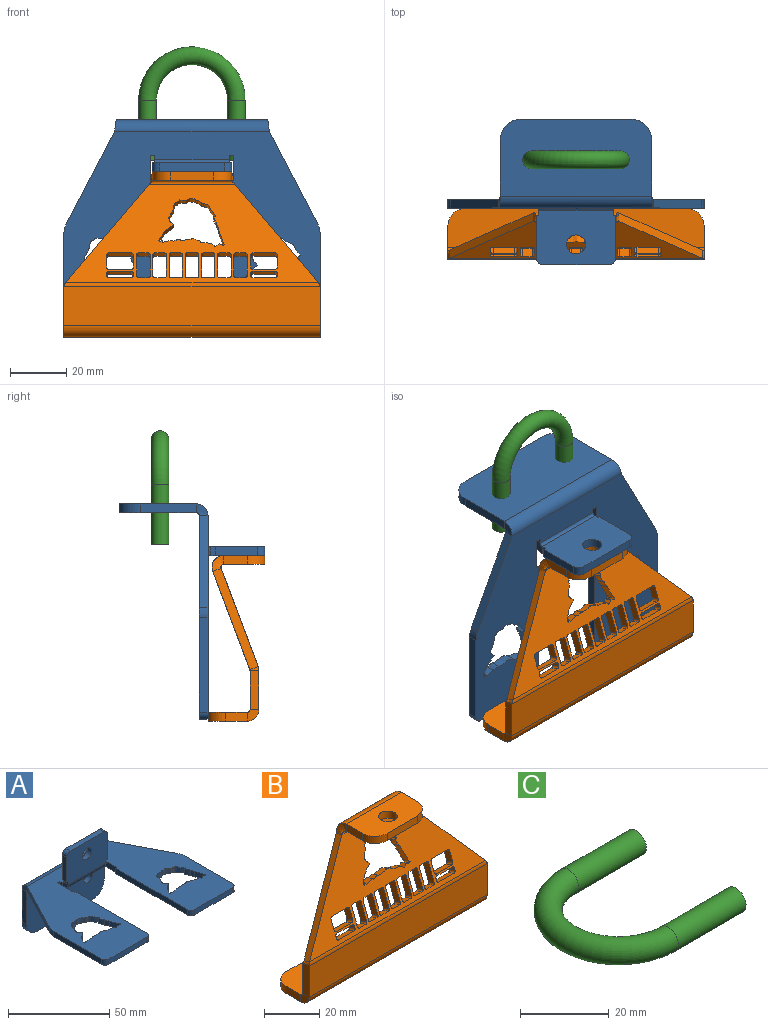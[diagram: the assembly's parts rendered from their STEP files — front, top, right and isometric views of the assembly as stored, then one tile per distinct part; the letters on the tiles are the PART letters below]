
ASSEMBLY  parts=3 mates=2
PART A: 137 faces, bbox 91.4x76.8x52.1 mm
  f0: extruded ~3.18x1.23mm, area 5mm2, adj f1,f118,f122,f127
  f1: extruded ~3.18x0.29mm, area 1.3mm2, adj f0,f2,f122,f127
  f2: plane 3.18x0.73mm, normal (0.99,-0.11,0), area 2.3mm2, adj f1,f3,f122,f127
  f3: plane 3.18x0.12mm, normal (0.16,-0.99,0), area 0.4mm2, adj f2,f4,f122,f127
  f4: extruded ~3.18x1.76mm, area 5.8mm2, adj f3,f5,f122,f127
  f5: extruded ~5.06x3.18mm, area 18.6mm2, adj f4,f6,f122,f127
  f6: plane 3.18x0.22mm, normal (-0.34,0.94,0), area 0.7mm2, adj f5,f7,f122,f127
  f7: plane 3.18x0.96mm, normal (0.85,0.53,0), area 3.6mm2, adj f6,f8,f122,f127
  f8: extruded ~3.67x3.18mm, area 14.9mm2, adj f7,f9,f122,f127
  f9: extruded ~3.37x3.18mm, area 12.2mm2, adj f8,f10,f122,f127
  f10: plane 3.18x0.41mm, normal (0.8,0.61,0), area 1.6mm2, adj f9,f11,f122,f127
  f11: extruded ~3.18x1.02mm, area 3.7mm2, adj f10,f12,f122,f127
  f12: extruded ~3.18x0.67mm, area 2.2mm2, adj f11,f13,f122,f127
  f13: plane 3.49x3.18mm, normal (-0.25,0.97,0), area 11.4mm2, adj f12,f14,f122,f127
  f14: plane 3.18x0.45mm, normal (0.69,0.72,0), area 2mm2, adj f13,f15,f122,f127
  f15: extruded ~3.18x2.35mm, area 7.8mm2, adj f14,f16,f122,f127
  f16: extruded ~7.55x3.18mm, area 26.4mm2, adj f15,f17,f122,f127
  f17: extruded ~3.18x0.31mm, area 1.1mm2, adj f16,f18,f122,f127
  f18: extruded ~5.49x3.18mm, area 19.8mm2, adj f17,f19,f122,f127
  f19: plane 3.18x1.27mm, normal (-0.64,0.77,0), area 5.3mm2, adj f18,f20,f122,f127
  f20: plane 3.18x1.51mm, normal (0.36,0.93,0), area 5.1mm2, adj f19,f21,f122,f127
  f21: plane 3.18x0.49mm, normal (-0.75,0.66,0), area 2.1mm2, adj f20,f22,f122,f127
  f22: extruded ~5.47x3.18mm, area 19mm2, adj f21,f23,f122,f127
  f23: plane 3.18x0.06mm, normal (-0.83,0.55,0), area 0.2mm2, adj f22,f24,f122,f127
  f24: plane 3.18x2.27mm, normal (-0.95,-0.33,0), area 7.6mm2, adj f23,f25,f122,f127
  f25: plane 3.18x0.08mm, normal (-0.71,0.71,0), area 0.4mm2, adj f24,f26,f122,f127
  f26: extruded ~3.18x2.84mm, area 10mm2, adj f25,f27,f122,f127
  f27: extruded ~3.18x0.8mm, area 3mm2, adj f26,f28,f122,f127
  f28: extruded ~4.31x3.18mm, area 16.9mm2, adj f27,f29,f122,f127
  f29: extruded ~3.18x1.2mm, area 3.9mm2, adj f28,f30,f122,f127
  f30: plane 3.18x0.16mm, normal (-0.89,-0.45,0), area 0.6mm2, adj f29,f31,f122,f127
  f31: plane 3.18x0.84mm, normal (-0.07,-1,0), area 2.7mm2, adj f30,f32,f122,f127
  f32: extruded ~3.18x1.27mm, area 5.5mm2, adj f31,f33,f122,f127
  f33: plane 3.18x0.04mm, normal (-0.89,0.45,0), area 0.1mm2, adj f32,f34,f122,f127
  f34: plane 3.18x0.76mm, normal (-0.34,-0.94,0), area 2.6mm2, adj f33,f35,f122,f127
  f35: plane 3.18x0.04mm, normal (-0.89,0.45,0), area 0.1mm2, adj f34,f36,f122,f127
  f36: extruded ~3.18x2.14mm, area 6.9mm2, adj f35,f37,f122,f127
  f37: plane 3.18x0.16mm, normal (-0.99,-0.12,0), area 0.5mm2, adj f36,f38,f122,f127
  f38: plane 3.18x0.2mm, normal (-0.51,-0.86,0), area 0.7mm2, adj f37,f39,f122,f127
  f39: extruded ~3.63x3.18mm, area 12.4mm2, adj f38,f40,f122,f127
  f40: plane 3.18x0.18mm, normal (0.91,-0.41,0), area 0.6mm2, adj f39,f118,f122,f127
  f41: plane 3.18x0.47mm, normal (-0.73,0.68,0), area 2mm2, adj f42,f117,f122,f127
  f42: extruded ~5.47x3.18mm, area 19mm2, adj f41,f43,f122,f127
  f43: plane 3.18x0.06mm, normal (-0.83,0.55,0), area 0.2mm2, adj f42,f44,f122,f127
  f44: plane 3.18x2.27mm, normal (-0.95,-0.33,0), area 7.6mm2, adj f43,f45,f122,f127
  f45: plane 3.18x0.08mm, normal (-0.71,0.71,0), area 0.4mm2, adj f44,f46,f122,f127
  f46: extruded ~3.18x2.84mm, area 10mm2, adj f45,f47,f122,f127
  f47: extruded ~3.18x0.8mm, area 3mm2, adj f46,f48,f122,f127
  f48: extruded ~4.31x3.18mm, area 16.9mm2, adj f47,f49,f122,f127
  f49: extruded ~3.18x1.2mm, area 3.9mm2, adj f48,f50,f122,f127
  f50: plane 3.18x0.16mm, normal (-0.89,-0.45,0), area 0.6mm2, adj f49,f51,f122,f127
  f51: plane 3.18x0.84mm, normal (-0.07,-1,0), area 2.7mm2, adj f50,f52,f122,f127
  f52: extruded ~3.18x1.27mm, area 5.5mm2, adj f51,f53,f122,f127
  f53: plane 3.18x0.04mm, normal (-0.89,0.45,0), area 0.1mm2, adj f52,f54,f122,f127
  f54: plane 3.18x0.76mm, normal (-0.34,-0.94,0), area 2.6mm2, adj f53,f55,f122,f127
  f55: plane 3.18x0.04mm, normal (-0.89,0.45,0), area 0.1mm2, adj f54,f56,f122,f127
  f56: extruded ~3.18x2.14mm, area 6.9mm2, adj f55,f57,f122,f127
  f57: plane 3.18x0.16mm, normal (-0.99,-0.12,0), area 0.5mm2, adj f56,f58,f122,f127
  f58: plane 3.18x0.2mm, normal (-0.51,-0.86,0), area 0.7mm2, adj f57,f59,f122,f127
  f59: extruded ~3.63x3.18mm, area 12.4mm2, adj f58,f60,f122,f127
  f60: plane 3.18x0.18mm, normal (0.91,-0.41,0), area 0.6mm2, adj f59,f61,f122,f127
  f61: plane 3.18x0.14mm, normal (-0.27,-0.96,0), area 0.5mm2, adj f60,f62,f122,f127
  f62: extruded ~3.18x1.24mm, area 5mm2, adj f61,f63,f122,f127
  f63: extruded ~3.18x0.29mm, area 1.3mm2, adj f62,f64,f122,f127
  f64: plane 3.18x0.73mm, normal (0.99,-0.11,0), area 2.3mm2, adj f63,f65,f122,f127
  f65: plane 3.18x0.12mm, normal (0.16,-0.99,0), area 0.4mm2, adj f64,f66,f122,f127
  f66: extruded ~3.18x1.76mm, area 5.8mm2, adj f65,f67,f122,f127
  f67: extruded ~5.06x3.18mm, area 18.6mm2, adj f66,f68,f122,f127
  f68: plane 3.18x0.22mm, normal (-0.34,0.94,0), area 0.7mm2, adj f67,f69,f122,f127
  f69: plane 3.18x0.96mm, normal (0.85,0.53,0), area 3.6mm2, adj f68,f70,f122,f127
  f70: extruded ~3.67x3.18mm, area 14.9mm2, adj f69,f71,f122,f127
  f71: extruded ~3.37x3.18mm, area 12.2mm2, adj f70,f72,f122,f127
  f72: plane 3.18x0.41mm, normal (0.8,0.61,0), area 1.6mm2, adj f71,f73,f122,f127
  f73: extruded ~3.18x1.02mm, area 3.7mm2, adj f72,f74,f122,f127
  f74: extruded ~3.18x0.67mm, area 2.2mm2, adj f73,f75,f122,f127
  f75: plane 3.49x3.18mm, normal (-0.25,0.97,0), area 11.4mm2, adj f74,f76,f122,f127
  f76: plane 3.18x0.45mm, normal (0.69,0.72,0), area 2mm2, adj f75,f77,f122,f127
  f77: extruded ~3.18x2.35mm, area 7.8mm2, adj f76,f78,f122,f127
  f78: extruded ~7.55x3.18mm, area 26.4mm2, adj f77,f79,f122,f127
  f79: extruded ~3.18x0.31mm, area 1.1mm2, adj f78,f80,f122,f127
  f80: extruded ~5.49x3.18mm, area 19.8mm2, adj f79,f81,f122,f127
  f81: plane 3.18x1.27mm, normal (-0.64,0.76,0), area 5.3mm2, adj f80,f117,f122,f127
  f82: plane 3.18x1.59mm, normal (-1,0,0), area 5mm2, adj f83,f119,f122,f127
  f83: plane 3.18x1.59mm, normal (0,-1,0), area 5mm2, adj f82,f84,f122,f127
  f84: plane 11.56x3.18mm, normal (1,0,0), area 36.7mm2, adj f83,f85,f122,f127
  f85: plane 3.18x0.79mm, normal (0,1,0), area 2.5mm2, adj f84,f86,f122,f127
  f86: plane 50.1x3.18mm, normal (1,0,0), area 159.1mm2, adj f85,f87,f122,f127
  f87: cylinder r=2.54mm len=3.18mm, axis (0,0,1), area 12.7mm2, adj f86,f88,f122,f127
  f88: plane 26.51x3.18mm, normal (0,-1,0), area 84.2mm2, adj f87,f89,f122,f127
  f89: cylinder r=2.54mm len=3.18mm, axis (0,0,1), area 12.7mm2, adj f88,f90,f122,f127
  f90: plane 33.68x3.18mm, normal (-1,0,0), area 106.9mm2, adj f89,f122,f127,f131
  f91: plane 32.88x17.24mm, normal (-0.89,0.46,0), area 117.9mm2, adj f92,f122,f127,f131
  f92: bspline ~5.02x4.76mm, area 13.1mm2, adj f91,f93,f124,f129
  f93: plane 19.94x3.18mm, normal (-1,0,0), area 63.3mm2, adj f92,f121,f126,f133
  f94: plane 38.91x3.18mm, normal (0,0,-1), area 123.5mm2, adj f121,f126,f132,f133
  f95: plane 19.94x3.18mm, normal (1,0,0), area 63.3mm2, adj f96,f121,f126,f132
  f96: bspline ~5.2x5.02mm, area 13.1mm2, adj f95,f97,f124,f129
  f97: plane 32.88x17.24mm, normal (0.89,0.46,0), area 117.9mm2, adj f96,f122,f127,f130
  f98: plane 33.68x3.18mm, normal (1,0,0), area 106.9mm2, adj f99,f122,f127,f130
  f99: cylinder r=2.54mm len=3.18mm, axis (0,0,1), area 12.7mm2, adj f98,f100,f122,f127
  f100: plane 26.51x3.18mm, normal (0,-1,0), area 84.2mm2, adj f99,f101,f122,f127
  f101: cylinder r=2.54mm len=3.18mm, axis (0,0,1), area 12.7mm2, adj f100,f102,f122,f127
  f102: plane 50.1x3.18mm, normal (-1,0,0), area 159.1mm2, adj f101,f103,f122,f127
  f103: plane 3.18x0.79mm, normal (0,1,0), area 2.5mm2, adj f102,f104,f122,f127
  f104: plane 11.56x3.18mm, normal (-1,0,0), area 36.7mm2, adj f103,f105,f122,f127
  f105: plane 3.18x1.59mm, normal (0,-1,0), area 5mm2, adj f104,f106,f122,f127
  f106: plane 3.18x1.59mm, normal (1,0,0), area 5mm2, adj f105,f107,f122,f127
  f107: plane 4.19x4.19mm, normal (1,0,0), area 13mm2, adj f106,f108,f123,f128
  f108: plane 3.18x1.59mm, normal (1,0,0), area 5mm2, adj f107,f109,f120,f125
  f109: plane 3.18x0.79mm, normal (0,0,-1), area 2.5mm2, adj f108,f110,f120,f125
  f110: plane 15.18x3.18mm, normal (1,0,0), area 48.2mm2, adj f109,f111,f120,f125
  f111: cylinder r=2.54mm len=3.18mm, axis (0,1,0), area 12.7mm2, adj f110,f112,f120,f125
  f112: plane 23.18x3.18mm, normal (0,0,1), area 73.6mm2, adj f111,f113,f120,f125
  f113: cylinder r=2.54mm len=3.18mm, axis (0,1,0), area 12.7mm2, adj f112,f114,f120,f125
  f114: plane 15.18x3.18mm, normal (-1,0,0), area 48.2mm2, adj f113,f115,f120,f125
  f115: plane 3.18x0.79mm, normal (0,0,-1), area 2.5mm2, adj f114,f116,f120,f125
  f116: plane 3.18x1.59mm, normal (-1,0,0), area 5mm2, adj f115,f119,f120,f125
  f117: plane 3.18x1.51mm, normal (0.36,0.93,0), area 5.1mm2, adj f41,f81,f122,f127
  f118: plane 3.18x0.14mm, normal (-0.27,-0.96,0), area 0.5mm2, adj f0,f40,f122,f127
  f119: plane 4.19x4.19mm, normal (-1,0,0), area 13mm2, adj f82,f116,f123,f128
  f120: plane 28.26x19.3mm, normal (0,-1,0), area 504.4mm2, adj f108,f109,f110,f111,f112,f113,f114,f115
  f121: plane 54.15x27.56mm, normal (0,-1,0), area 1415.7mm2, adj f93,f94,f95,f124,f132,f133,f134,f135
  f122: plane 91.44x72.64mm, normal (0,0,-1), area 3734.6mm2, adj f0,f1,f2,f3,f4,f5,f6,f7
  f123: cylinder r=4.19mm len=26.68mm, axis (1,0,0), area 175.6mm2, adj f107,f119,f120,f122
  f124: cylinder r=1.02mm len=55.22mm, axis (1,0,0), area 87mm2, adj f92,f96,f121,f122
  f125: plane 28.26x19.3mm, normal (0,1,0), area 504.4mm2, adj f108,f109,f110,f111,f112,f113,f114,f115
  f126: plane 54.15x27.56mm, normal (0,1,0), area 1415.7mm2, adj f93,f94,f95,f129,f132,f133,f134,f135
  f127: plane 91.44x72.64mm, normal (0,0,1), area 3734.6mm2, adj f0,f1,f2,f3,f4,f5,f6,f7
  f128: cylinder r=1.02mm len=26.68mm, axis (1,0,0), area 42.6mm2, adj f107,f119,f125,f127
  f129: cylinder r=4.19mm len=55.22mm, axis (1,0,0), area 359mm2, adj f92,f96,f126,f127
  f130: cylinder r=7.62mm len=3.54mm, axis (0,0,1), area 11.7mm2, adj f97,f98,f122,f127
  f131: cylinder r=7.62mm len=3.54mm, axis (0,0,-1), area 11.7mm2, adj f90,f91,f122,f127
  f132: cylinder r=7.62mm len=7.62mm, axis (0,-1,0), area 38mm2, adj f94,f95,f121,f126
  f133: cylinder r=7.62mm len=7.62mm, axis (0,1,0), area 38mm2, adj f93,f94,f121,f126
  f134: cylinder r=2.87mm len=5.74mm, axis (0,1,0), area 57.3mm2, adj f121,f126
  f135: cylinder r=2.87mm len=5.74mm, axis (0,1,0), area 57.3mm2, adj f121,f126
  f136: cylinder r=3.38mm len=6.76mm, axis (0,1,0), area 67.4mm2, adj f120,f125
PART B: 165 faces, bbox 91.4x20.6x59.1 mm
  f0: bspline ~5.67x4.19mm, area 16.5mm2, adj f3,f16,f22,f163
  f1: bspline ~6.5x5.91mm, area 16.5mm2, adj f3,f6,f22,f164
  f2: plane 28.26x14.68mm, normal (0,0,1), area 361.9mm2, adj f3,f4,f5,f17,f118,f163,f164
  f3: cylinder r=4.19mm len=30.6mm, axis (1,0,0), area 235.9mm2, adj f0,f1,f2,f25
  f4: cylinder r=6.35mm len=6.35mm, axis (0,0,1), area 31.7mm2, adj f2,f17,f18,f163
  f5: cylinder r=6.35mm len=6.35mm, axis (0,0,1), area 31.7mm2, adj f2,f17,f18,f164
  f6: plane 36.22x29.81mm, normal (-0.78,0.22,0.58), area 152.1mm2, adj f1,f7,f19,f25
  f7: bspline ~3.26x1.64mm, area 3.7mm2, adj f6,f8,f23,f28
  f8: plane 13.8x3.18mm, normal (-1,0,0), area 43.8mm2, adj f7,f9,f20,f26
  f9: plane 4.19x4.19mm, normal (-1,0,0), area 13mm2, adj f8,f10,f24,f29
  f10: plane 7.63x3.18mm, normal (-1,0,0), area 24.2mm2, adj f9,f21,f27,f162
  f11: plane 78.74x3.18mm, normal (0,1,0), area 250mm2, adj f21,f27,f161,f162
  f12: plane 7.63x3.18mm, normal (1,0,0), area 24.2mm2, adj f13,f21,f27,f161
  f13: plane 4.19x4.19mm, normal (1,0,0), area 13mm2, adj f12,f14,f24,f29
  f14: plane 13.8x3.18mm, normal (1,0,0), area 43.8mm2, adj f13,f15,f20,f26
  f15: bspline ~3.26x1.77mm, area 3.7mm2, adj f14,f16,f23,f28
  f16: plane 36.22x29.81mm, normal (0.78,0.22,0.58), area 152.1mm2, adj f0,f15,f19,f25
  f17: plane 15.56x3.18mm, normal (0,-1,0), area 49.4mm2, adj f2,f4,f5,f18
  f18: plane 28.26x14.68mm, normal (0,0,-1), area 361.9mm2, adj f4,f5,f17,f22,f118,f163,f164
  f19: plane 90.23x35.1mm, normal (0,-0.94,0.35), area 1523mm2, adj f6,f16,f22,f23,f30,f31,f32,f33
  f20: plane 91.44x13.8mm, normal (0,-1,0), area 1261.8mm2, adj f8,f14,f23,f24
  f21: plane 91.44x13.98mm, normal (0,0,-1), area 1261.4mm2, adj f10,f11,f12,f24,f161,f162
  f22: cylinder r=1.02mm len=30.6mm, axis (1,0,0), area 57.2mm2, adj f0,f1,f18,f19
  f23: cylinder r=4.19mm len=91.44mm, axis (-1,0,0), area 137.4mm2, adj f7,f15,f19,f20
  f24: cylinder r=4.19mm len=91.44mm, axis (-1,0,0), area 602mm2, adj f9,f13,f20,f21
  f25: plane 90.23x35.1mm, normal (0,0.94,-0.35), area 1518.8mm2, adj f3,f6,f16,f28,f30,f31,f32,f33
  f26: plane 91.44x13.8mm, normal (0,1,0), area 1261.8mm2, adj f8,f14,f28,f29
  f27: plane 91.44x13.98mm, normal (0,0,1), area 1261.4mm2, adj f10,f11,f12,f29,f161,f162
  f28: cylinder r=1.02mm len=91.44mm, axis (-1,0,0), area 33.3mm2, adj f7,f15,f25,f26
  f29: cylinder r=1.02mm len=91.44mm, axis (-1,0,0), area 145.9mm2, adj f9,f13,f26,f27
  f30: plane 3.37x2.97mm, normal (0,0.35,0.94), area 10.7mm2, adj f19,f25,f31,f37
  f31: cylinder r=0.69mm len=3.21mm, axis (0,-0.94,0.35), area 3.4mm2, adj f19,f25,f30,f32
  f32: plane 8.76x5.85mm, normal (-1,0,0), area 25.9mm2, adj f19,f25,f31,f33
  f33: cylinder r=0.69mm len=3.21mm, axis (0,-0.94,0.35), area 3.4mm2, adj f19,f25,f32,f34
  f34: plane 3.37x2.97mm, normal (0,-0.35,-0.94), area 10.7mm2, adj f19,f25,f33,f35
  f35: cylinder r=0.69mm len=3.21mm, axis (0,-0.94,0.35), area 3.4mm2, adj f19,f25,f34,f36
  f36: plane 8.76x5.85mm, normal (1,0,0), area 25.9mm2, adj f19,f25,f35,f37
  f37: cylinder r=0.69mm len=3.21mm, axis (0,-0.94,0.35), area 3.4mm2, adj f19,f25,f30,f36
  f38: plane 3.37x2.97mm, normal (0,-0.35,-0.94), area 10.7mm2, adj f19,f25,f39,f45
  f39: cylinder r=0.69mm len=3.21mm, axis (0,-0.94,0.35), area 3.4mm2, adj f19,f25,f38,f40
  f40: plane 8.76x5.85mm, normal (1,0,0), area 25.9mm2, adj f19,f25,f39,f41
  f41: cylinder r=0.69mm len=3.21mm, axis (0,-0.94,0.35), area 3.4mm2, adj f19,f25,f40,f42
  f42: plane 3.37x2.97mm, normal (0,0.35,0.94), area 10.7mm2, adj f19,f25,f41,f43
  f43: cylinder r=0.69mm len=3.21mm, axis (0,-0.94,0.35), area 3.4mm2, adj f19,f25,f42,f44
  f44: plane 8.76x5.85mm, normal (-1,0,0), area 25.9mm2, adj f19,f25,f43,f45
  f45: cylinder r=0.69mm len=3.21mm, axis (0,-0.94,0.35), area 3.4mm2, adj f19,f25,f38,f44
  f46: plane 8.76x5.85mm, normal (1,0,0), area 25.9mm2, adj f19,f25,f47,f53
  f47: cylinder r=0.69mm len=3.21mm, axis (0,-0.94,0.35), area 3.4mm2, adj f19,f25,f46,f48
  f48: plane 3.37x2.97mm, normal (0,0.35,0.94), area 10.7mm2, adj f19,f25,f47,f49
  f49: cylinder r=0.69mm len=3.21mm, axis (0,-0.94,0.35), area 3.4mm2, adj f19,f25,f48,f50
  f50: plane 8.76x5.85mm, normal (-1,0,0), area 25.9mm2, adj f19,f25,f49,f51
  f51: cylinder r=0.69mm len=3.21mm, axis (0,-0.94,0.35), area 3.4mm2, adj f19,f25,f50,f52
  f52: plane 3.37x2.97mm, normal (0,-0.35,-0.94), area 10.7mm2, adj f19,f25,f51,f53
  f53: cylinder r=0.69mm len=3.21mm, axis (0,-0.94,0.35), area 3.4mm2, adj f19,f25,f46,f52
  f54: plane 3.37x2.97mm, normal (0,0.35,0.94), area 10.7mm2, adj f19,f25,f55,f61
  f55: cylinder r=0.69mm len=3.21mm, axis (0,-0.94,0.35), area 3.4mm2, adj f19,f25,f54,f56
  f56: plane 8.76x5.85mm, normal (-1,0,0), area 25.9mm2, adj f19,f25,f55,f57
  f57: cylinder r=0.69mm len=3.21mm, axis (0,-0.94,0.35), area 3.4mm2, adj f19,f25,f56,f58
  f58: plane 3.37x2.97mm, normal (0,-0.35,-0.94), area 10.7mm2, adj f19,f25,f57,f59
  f59: cylinder r=0.69mm len=3.21mm, axis (0,-0.94,0.35), area 3.4mm2, adj f19,f25,f58,f60
  f60: plane 8.76x5.85mm, normal (1,0,0), area 25.9mm2, adj f19,f25,f59,f61
  f61: cylinder r=0.69mm len=3.21mm, axis (0,-0.94,0.35), area 3.4mm2, adj f19,f25,f54,f60
  f62: plane 3.37x2.97mm, normal (0,0.35,0.94), area 10.7mm2, adj f19,f25,f63,f69
  f63: cylinder r=0.69mm len=3.21mm, axis (0,-0.94,0.35), area 3.4mm2, adj f19,f25,f62,f64
  f64: plane 8.76x5.85mm, normal (-1,0,0), area 25.9mm2, adj f19,f25,f63,f65
  f65: cylinder r=0.69mm len=3.21mm, axis (0,-0.94,0.35), area 3.4mm2, adj f19,f25,f64,f66
  f66: plane 3.37x2.97mm, normal (0,-0.35,-0.94), area 10.7mm2, adj f19,f25,f65,f67
  f67: cylinder r=0.69mm len=3.21mm, axis (0,-0.94,0.35), area 3.4mm2, adj f19,f25,f66,f68
  f68: plane 8.76x5.85mm, normal (1,0,0), area 25.9mm2, adj f19,f25,f67,f69
  f69: cylinder r=0.69mm len=3.21mm, axis (0,-0.94,0.35), area 3.4mm2, adj f19,f25,f62,f68
  f70: plane 3.37x2.97mm, normal (0,-0.35,-0.94), area 10.7mm2, adj f19,f25,f71,f77
  f71: cylinder r=0.69mm len=3.21mm, axis (0,-0.94,0.35), area 3.4mm2, adj f19,f25,f70,f72
  f72: plane 8.76x5.85mm, normal (1,0,0), area 25.9mm2, adj f19,f25,f71,f73
  f73: cylinder r=0.69mm len=3.21mm, axis (0,-0.94,0.35), area 3.4mm2, adj f19,f25,f72,f74
  f74: plane 3.37x2.97mm, normal (0,0.35,0.94), area 10.7mm2, adj f19,f25,f73,f75
  f75: cylinder r=0.69mm len=3.21mm, axis (0,-0.94,0.35), area 3.4mm2, adj f19,f25,f74,f76
  f76: plane 8.76x5.85mm, normal (-1,0,0), area 25.9mm2, adj f19,f25,f75,f77
  f77: cylinder r=0.69mm len=3.21mm, axis (0,-0.94,0.35), area 3.4mm2, adj f19,f25,f70,f76
  f78: plane 3.37x2.97mm, normal (0,-0.35,-0.94), area 10.7mm2, adj f19,f25,f79,f85
  f79: cylinder r=0.69mm len=3.21mm, axis (0,-0.94,0.35), area 3.4mm2, adj f19,f25,f78,f80
  f80: plane 8.76x5.85mm, normal (1,0,0), area 25.9mm2, adj f19,f25,f79,f81
  f81: cylinder r=0.69mm len=3.21mm, axis (0,-0.94,0.35), area 3.4mm2, adj f19,f25,f80,f82
  f82: plane 3.37x2.97mm, normal (0,0.35,0.94), area 10.7mm2, adj f19,f25,f81,f83
  f83: cylinder r=0.69mm len=3.21mm, axis (0,-0.94,0.35), area 3.4mm2, adj f19,f25,f82,f84
  f84: plane 8.76x5.85mm, normal (-1,0,0), area 25.9mm2, adj f19,f25,f83,f85
  f85: cylinder r=0.69mm len=3.21mm, axis (0,-0.94,0.35), area 3.4mm2, adj f19,f25,f78,f84
  f86: plane 7.81x2.97mm, normal (0,0.35,0.94), area 24.8mm2, adj f19,f25,f87,f93
  f87: cylinder r=0.86mm len=3.27mm, axis (0,-0.94,0.35), area 4.3mm2, adj f19,f25,f86,f88
  f88: plane 5.35x4.57mm, normal (-1,0,0), area 14.4mm2, adj f19,f25,f87,f89
  f89: cylinder r=0.86mm len=3.27mm, axis (0,-0.94,0.35), area 4.3mm2, adj f19,f25,f88,f90
  f90: plane 7.81x2.97mm, normal (0,-0.35,-0.94), area 24.8mm2, adj f19,f25,f89,f91
  f91: cylinder r=0.86mm len=3.27mm, axis (0,-0.94,0.35), area 4.3mm2, adj f19,f25,f90,f92
  f92: plane 5.35x4.57mm, normal (1,0,0), area 14.4mm2, adj f19,f25,f91,f93
  f93: cylinder r=0.86mm len=3.27mm, axis (0,-0.94,0.35), area 4.3mm2, adj f19,f25,f86,f92
  f94: plane 7.81x2.97mm, normal (0,0.35,0.94), area 24.8mm2, adj f19,f25,f95,f101
  f95: cylinder r=0.86mm len=3.27mm, axis (0,-0.94,0.35), area 4.3mm2, adj f19,f25,f94,f96
  f96: plane 5.35x4.57mm, normal (-1,0,0), area 14.4mm2, adj f19,f25,f95,f97
  f97: cylinder r=0.86mm len=3.27mm, axis (0,-0.94,0.35), area 4.3mm2, adj f19,f25,f96,f98
  f98: plane 7.81x2.97mm, normal (0,-0.35,-0.94), area 24.8mm2, adj f19,f25,f97,f99
  f99: cylinder r=0.86mm len=3.27mm, axis (0,-0.94,0.35), area 4.3mm2, adj f19,f25,f98,f100
  f100: plane 5.35x4.57mm, normal (1,0,0), area 14.4mm2, adj f19,f25,f99,f101
  f101: cylinder r=0.86mm len=3.27mm, axis (0,-0.94,0.35), area 4.3mm2, adj f19,f25,f94,f100
  f102: plane 7.81x2.97mm, normal (0,-0.35,-0.94), area 24.8mm2, adj f19,f25,f103,f109
  f103: cylinder r=0.86mm len=3.27mm, axis (0,-0.94,0.35), area 4.3mm2, adj f19,f25,f102,f104
  f104: plane 3.26x1.89mm, normal (1,0,0), area 2.6mm2, adj f19,f25,f103,f105
  f105: cylinder r=0.86mm len=3.27mm, axis (0,-0.94,0.35), area 4.3mm2, adj f19,f25,f104,f106
  f106: plane 7.81x2.97mm, normal (0,0.35,0.94), area 24.8mm2, adj f19,f25,f105,f107
  f107: cylinder r=0.86mm len=3.27mm, axis (0,-0.94,0.35), area 4.3mm2, adj f19,f25,f106,f108
  f108: plane 3.26x1.89mm, normal (-1,0,0), area 2.6mm2, adj f19,f25,f107,f109
  f109: cylinder r=0.86mm len=3.27mm, axis (0,-0.94,0.35), area 4.3mm2, adj f19,f25,f102,f108
  f110: plane 7.81x2.97mm, normal (0,-0.35,-0.94), area 24.8mm2, adj f19,f25,f111,f117
  f111: cylinder r=0.86mm len=3.27mm, axis (0,-0.94,0.35), area 4.3mm2, adj f19,f25,f110,f112
  f112: plane 3.26x1.89mm, normal (1,0,0), area 2.6mm2, adj f19,f25,f111,f113
  f113: cylinder r=0.86mm len=3.27mm, axis (0,-0.94,0.35), area 4.3mm2, adj f19,f25,f112,f114
  f114: plane 7.81x2.97mm, normal (0,0.35,0.94), area 24.8mm2, adj f19,f25,f113,f115
  f115: cylinder r=0.86mm len=3.27mm, axis (0,-0.94,0.35), area 4.3mm2, adj f19,f25,f114,f116
  f116: plane 3.26x1.89mm, normal (-1,0,0), area 2.6mm2, adj f19,f25,f115,f117
  f117: cylinder r=0.86mm len=3.27mm, axis (0,-0.94,0.35), area 4.3mm2, adj f19,f25,f110,f116
  f118: cylinder r=3.38mm len=6.76mm, axis (0,0,1), area 67.4mm2, adj f2,f18
  f119: plane 3.03x1.28mm, normal (0.91,-0.14,-0.38), area 0.6mm2, adj f19,f25,f120,f160
  f120: plane 2.98x1.16mm, normal (-0.27,-0.34,-0.9), area 0.4mm2, adj f19,f25,f119,f121
  f121: extruded ~3.25x1.86mm, area 4.9mm2, adj f19,f25,f120,f122
  f122: extruded ~3.06x1.35mm, area 1.2mm2, adj f19,f25,f121,f123
  f123: plane 3.22x1.78mm, normal (0.99,-0.04,-0.1), area 2.3mm2, adj f19,f25,f122,f124
  f124: plane 2.98x1.14mm, normal (0.16,-0.35,-0.92), area 0.4mm2, adj f19,f25,f123,f125
  f125: extruded ~3.58x2.74mm, area 5.6mm2, adj f19,f25,f124,f126
  f126: extruded ~5.75x4.72mm, area 18.2mm2, adj f19,f25,f125,f127
  f127: plane 3x1.19mm, normal (-0.34,0.33,0.88), area 0.7mm2, adj f19,f25,f126,f128
  f128: plane 3.3x2mm, normal (0.85,0.19,0.5), area 3.5mm2, adj f19,f25,f127,f129
  f129: extruded ~3.99x3.81mm, area 14.6mm2, adj f19,f25,f128,f130
  f130: extruded ~4.21x4.14mm, area 12mm2, adj f19,f25,f129,f131
  f131: plane 3.11x1.5mm, normal (0.8,0.21,0.57), area 1.6mm2, adj f19,f25,f130,f132
  f132: extruded ~3.14x1.57mm, area 3.6mm2, adj f19,f25,f131,f133
  f133: extruded ~3.2x1.73mm, area 2.1mm2, adj f19,f25,f132,f134
  f134: plane 3.42x3.28mm, normal (-0.25,0.34,0.91), area 11.2mm2, adj f19,f25,f133,f135
  f135: plane 3.12x1.51mm, normal (0.69,0.25,0.68), area 1.9mm2, adj f19,f25,f134,f136
  f136: extruded ~3.18x2.3mm, area 7.7mm2, adj f19,f25,f135,f137
  f137: extruded ~7.39x3.31mm, area 25.8mm2, adj f19,f25,f136,f138
  f138: extruded ~3.08x1.41mm, area 1mm2, adj f19,f25,f137,f139
  f139: extruded ~5.38x3.58mm, area 19.4mm2, adj f19,f25,f138,f140
  f140: plane 3.34x2.09mm, normal (-0.64,0.27,0.72), area 5.2mm2, adj f19,f25,f139,f141
  f141: plane 3.17x1.66mm, normal (0.36,0.33,0.87), area 5mm2, adj f19,f25,f140,f142
  f142: plane 3.14x1.57mm, normal (-0.75,0.23,0.62), area 2mm2, adj f19,f25,f141,f143
  f143: extruded ~6.13x4.86mm, area 18.6mm2, adj f19,f25,f142,f144
  f144: plane 2.99x1.17mm, normal (-0.83,0.2,0.52), area 0.2mm2, adj f19,f25,f143,f145
  f145: plane 3.76x3.2mm, normal (-0.95,-0.11,-0.31), area 7.5mm2, adj f19,f25,f144,f146
  f146: plane 3x1.19mm, normal (-0.71,0.25,0.66), area 0.3mm2, adj f19,f25,f145,f147
  f147: extruded ~3.95x3.72mm, area 9.8mm2, adj f19,f25,f146,f148
  f148: extruded ~3.12x1.51mm, area 2.9mm2, adj f19,f25,f147,f149
  f149: extruded ~5.07x4.46mm, area 16.5mm2, adj f19,f25,f148,f150
  f150: extruded ~3.05x1.34mm, area 3.8mm2, adj f19,f25,f149,f151
  f151: plane 3.03x1.26mm, normal (-0.89,-0.16,-0.42), area 0.5mm2, adj f19,f25,f150,f152
  f152: plane 2.99x1.17mm, normal (-0.07,-0.35,-0.93), area 2.6mm2, adj f19,f25,f151,f153
  f153: extruded ~3.36x2.16mm, area 5.4mm2, adj f19,f25,f152,f154
  f154: plane 2.98x1.16mm, normal (-0.89,0.16,0.42), area 0.1mm2, adj f19,f25,f153,f155
  f155: plane 3.07x1.37mm, normal (-0.34,-0.33,-0.88), area 2.5mm2, adj f19,f25,f154,f156
  f156: plane 2.98x1.16mm, normal (-0.89,0.16,0.42), area 0.1mm2, adj f19,f25,f155,f157
  f157: extruded ~3.07x2.09mm, area 6.8mm2, adj f19,f25,f156,f158
  f158: plane 3.03x1.26mm, normal (-0.99,-0.04,-0.12), area 0.5mm2, adj f19,f25,f157,f159
  f159: plane 3.01x1.23mm, normal (-0.51,-0.3,-0.8), area 0.7mm2, adj f19,f25,f158,f160
  f160: extruded ~3.55x3.28mm, area 12.2mm2, adj f19,f25,f119,f159
  f161: cylinder r=6.35mm len=6.35mm, axis (0,0,-1), area 31.7mm2, adj f11,f12,f21,f27
  f162: cylinder r=6.35mm len=6.35mm, axis (0,0,1), area 31.7mm2, adj f10,f11,f21,f27
  f163: plane 8.33x3.18mm, normal (1,0,0), area 26.5mm2, adj f0,f2,f4,f18
  f164: plane 8.33x3.18mm, normal (-1,0,0), area 26.5mm2, adj f1,f2,f5,f18
PART C: 5 faces, bbox 42.2x41.2x6.4 mm
  f0: cylinder r=3.17mm len=21.59mm, axis (1,0,0), area 430.7mm2, adj f1,f3
  f1: torus R=15.88mm, axis (0,0,-1), area 994.9mm2, adj f0,f2
  f2: cylinder r=3.17mm len=21.59mm, axis (1,0,0), area 430.7mm2, adj f1,f4
  f3: plane 6.35x6.35mm, normal (1,0,0), area 31.7mm2, adj f0
  f4: plane 6.35x6.35mm, normal (1,0,0), area 31.7mm2, adj f2
PLACE A rot(axis=(1,0,0),90deg) t=(7.5,3.18,36.42)mm
PLACE B at identity fixed
PLACE C rot(axis=(-0.58,0.58,0.58),120deg) t=(45.72,17.15,62.11)mm
MATE slider A.f135 <-> C.f2  axis (0,0,1) through (61.6,17.15,55.06)mm
MATE fastened A.f136 <-> B.f118  axis (0,0,-1) through (45.72,-12.98,36.65)mm
